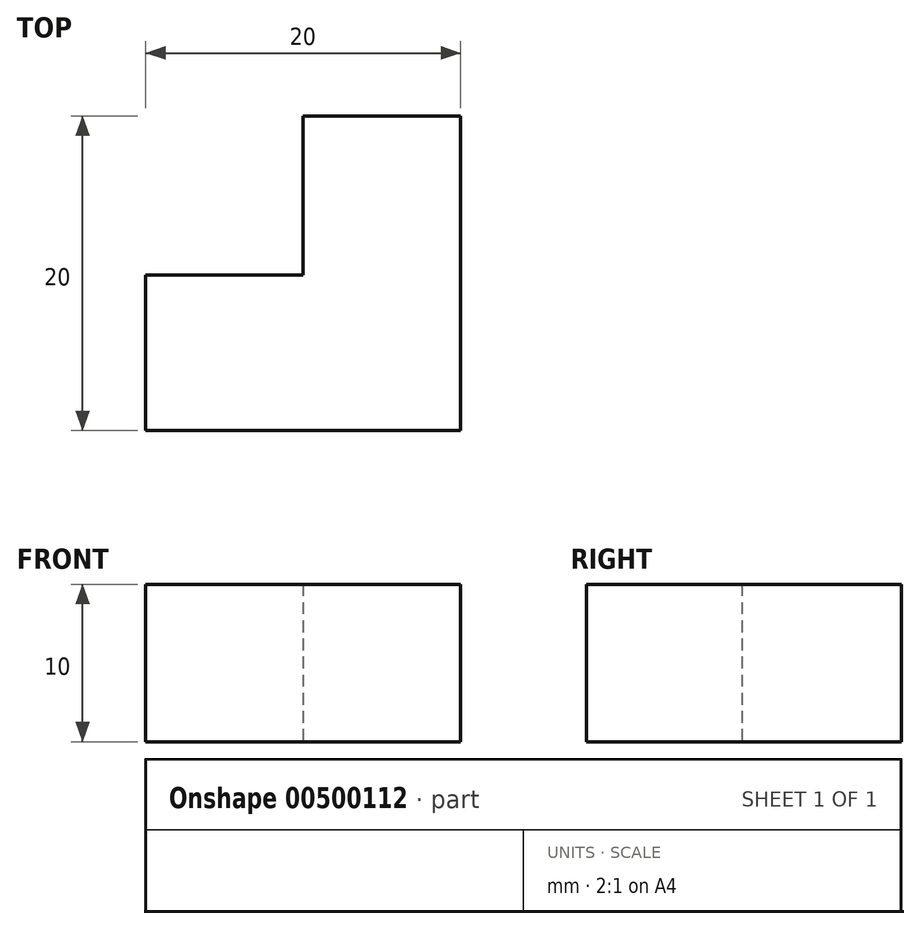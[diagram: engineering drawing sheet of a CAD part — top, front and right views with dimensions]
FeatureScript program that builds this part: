
annotation { "Feature Type Name" : "Feature", "Feature Type Description" : "" }
export const myFeature = defineFeature(function(context is Context, id is Id, definition is map)
    precondition{}
    {
        {
            var Q0;
            Q0=qCreatedBy(makeId("Top.planeOp"),FACE);
            var sketch = newSketch(context, id + "F0", { "sketchPlane" : qUnion([Q0])});
            skLineSegment(sketch, "E0", {"start": v(0, 0) * mm, "end": v(20, 0) * mm});
            skLineSegment(sketch, "E1", {"start": v(20, 0) * mm, "end": v(20, 20) * mm});
            skLineSegment(sketch, "E2", {"start": v(20, 20) * mm, "end": v(10, 20) * mm});
            skLineSegment(sketch, "E3", {"start": v(10, 20) * mm, "end": v(10, 9.88) * mm});
            skLineSegment(sketch, "E4", {"start": v(10, 9.88) * mm, "end": v(0, 9.88) * mm});
            skLineSegment(sketch, "E5", {"start": v(0, 9.88) * mm, "end": v(0, 0) * mm});
            skSolve(sketch);
        }
        {
            var Q0;
            Q0=makeQuery(id+"F0.imprint","IMPRINT",FACE,{"disambiguationData":[TD([[makeQuery(id+"F0.imprint","IMPRINT",EDGE,{"derivedFrom":sQuery(id+"F0.wireOp",EDGE,"E0")}),1.0]])]});
            extrude(context, id + "F1", {"entities" : qUnion([Q0]), "depth" : 10 * mm});
        }
    });
